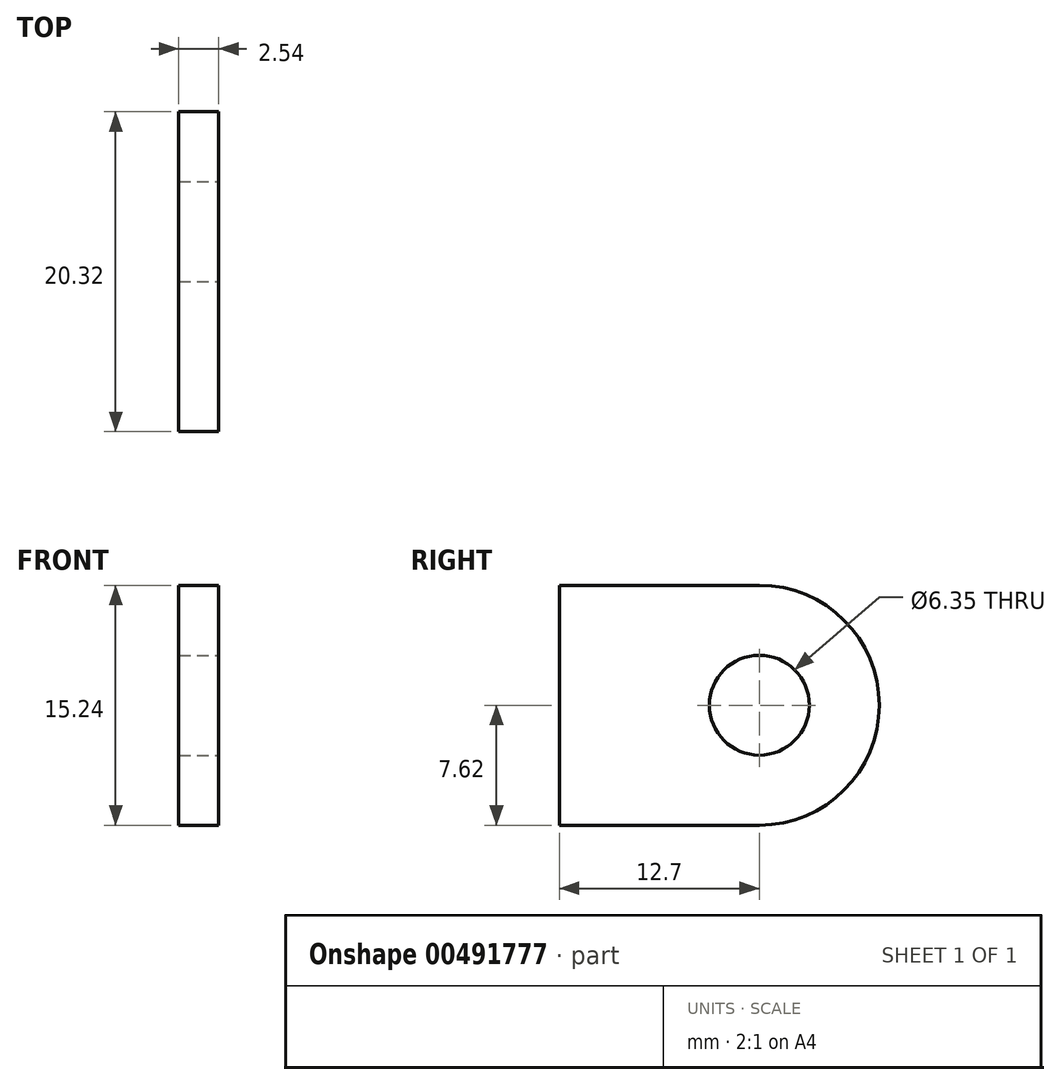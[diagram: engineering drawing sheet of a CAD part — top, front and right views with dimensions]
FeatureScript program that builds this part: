
annotation { "Feature Type Name" : "Feature", "Feature Type Description" : "" }
export const myFeature = defineFeature(function(context is Context, id is Id, definition is map)
    precondition{}
    {
        {
            var Q0;
            Q0=qCreatedBy(makeId("Right.planeOp"),FACE);
            var sketch = newSketch(context, id + "F0", { "sketchPlane" : qUnion([Q0])});
            skLineSegment(sketch, "E0", {"start": v(0, 0) * mm, "end": v(0, 15.24) * mm});
            skLineSegment(sketch, "E1", {"start": v(0, 15.24) * mm, "end": v(12.7, 15.24) * mm});
            skLineSegment(sketch, "E2", {"start": v(0, 0) * mm, "end": v(12.7, 0) * mm});
            skArc(sketch, "E3", {"start": v(12.7, 15.24) * mm, "mid": v(20.32, 7.62) * mm, "end": v(12.7, 0) * mm});
            skCircle(sketch, "E4", {"center": v(12.7, 7.62) * mm, "radius": 3.18 * mm});
            skSolve(sketch);
        }
        {
            var Q0;
            Q0=makeQuery(id+"F0.imprint","IMPRINT",FACE,{"disambiguationData":[TD([[makeQuery(id+"F0.imprint","IMPRINT",EDGE,{"derivedFrom":sQuery(id+"F0.wireOp",EDGE,"E0")}),-1.0]])]});
            extrude(context, id + "F1", {"entities" : qUnion([Q0]), "oppositeDirection" : true, "depth" : 2.54 * mm});
        }
    });
